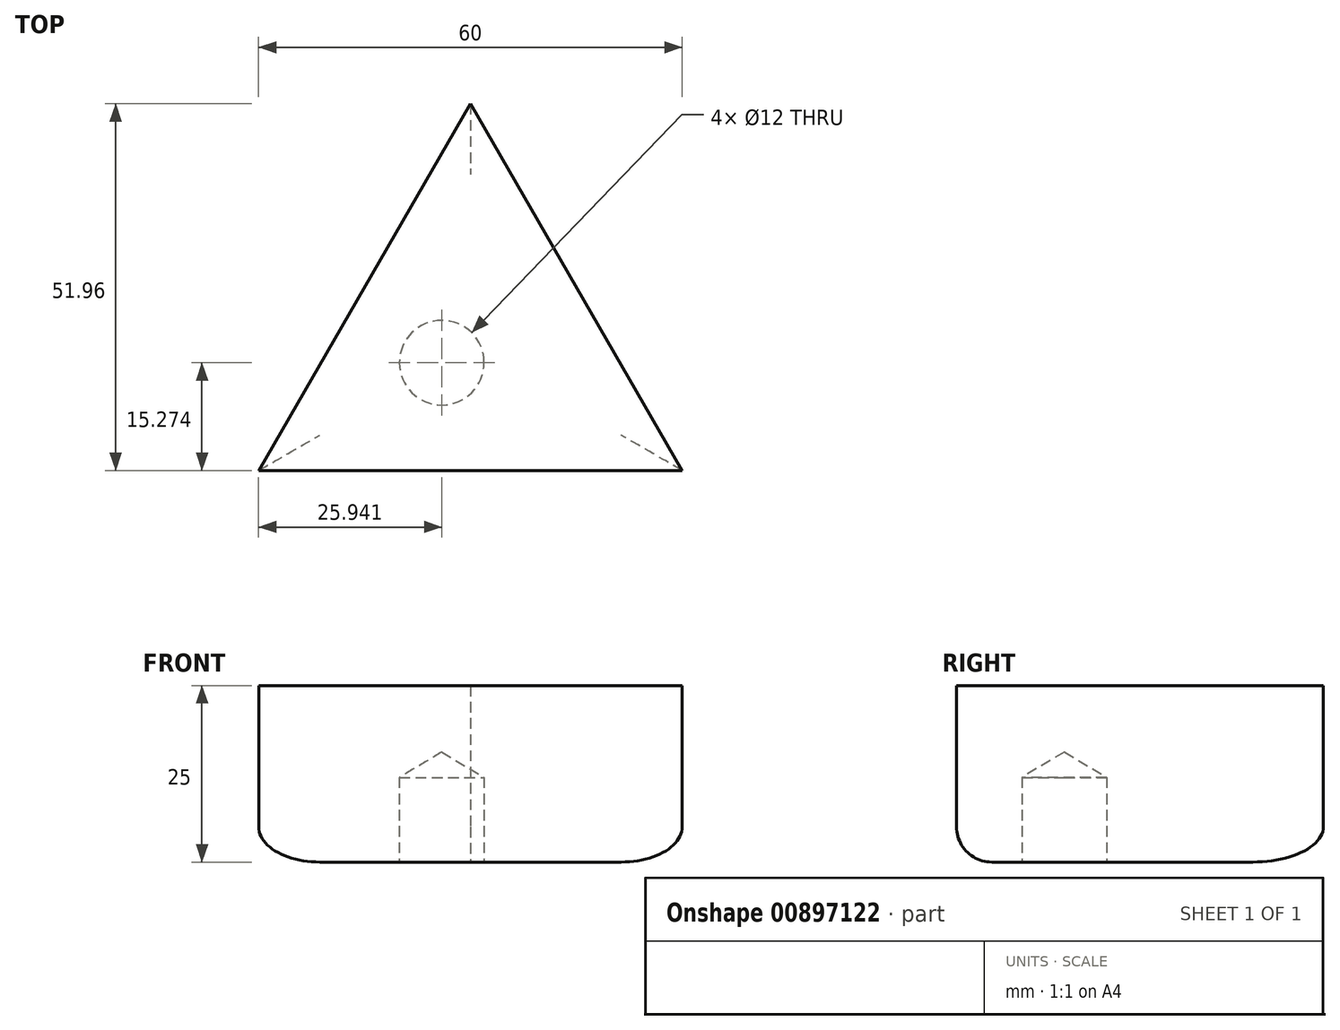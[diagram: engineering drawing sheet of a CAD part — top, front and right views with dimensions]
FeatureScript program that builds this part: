
annotation { "Feature Type Name" : "Feature", "Feature Type Description" : "" }
export const myFeature = defineFeature(function(context is Context, id is Id, definition is map)
    precondition{}
    {
        {
            var Q0;
            Q0=qCreatedBy(makeId("Top.planeOp"),FACE);
            var sketch = newSketch(context, id + "F0", { "sketchPlane" : qUnion([Q0])});
            skLineSegment(sketch, "E0", {"start": v(-14.06, 34.52) * mm, "end": v(-44.06, -17.44) * mm});
            skLineSegment(sketch, "E1", {"start": v(-44.06, -17.44) * mm, "end": v(15.94, -17.44) * mm});
            skLineSegment(sketch, "E2", {"start": v(15.94, -17.44) * mm, "end": v(-14.06, 34.52) * mm});
            skLineSegment(sketch, "E3", {"start": v(0.94, 8.54) * mm, "end": v(-44.06, -17.44) * mm, "construction": true});
            skLineSegment(sketch, "E4", {"start": v(-14.06, 34.52) * mm, "end": v(-21.56, -4.45) * mm, "construction": true});
            skLineSegment(sketch, "E5", {"start": v(-21.56, -4.45) * mm, "end": v(15.94, -17.44) * mm, "construction": true});
            skCircle(sketch, "E6", {"center": v(-21.56, -4.45) * mm, "radius": 7.39 * mm});
            skSolve(sketch);
        }
        {
            var Q0;
            Q0 = qSketchRegion(id + "F0", true);
            var Q1;
            Q1=makeQuery(id+"F0.imprint","IMPRINT",FACE,{"disambiguationData":[TD([[makeQuery(id+"F0.imprint","IMPRINT",EDGE,{"derivedFrom":sQuery(id+"F0.wireOp",EDGE,"E6")}),1.0]])]});
            extrude(context, id + "F1", {"entities" : qUnion([Q0, Q1]), "depth" : 25 * mm, "offsetDistance" : 25 * mm});
        }
        {
            var Q0;
            Q0=qCreatedBy(makeId("Top.planeOp"),FACE);
            var sketch = newSketch(context, id + "F2", { "sketchPlane" : qUnion([Q0])});
            skCircle(sketch, "E7", {"center": v(-18.12, -2.17) * mm, "radius": 6.2 * mm});
            skSolve(sketch);
        }
        {
            var Q0;
            Q0=sQuery(id+"F2.wireOp",VERTEX,"E7.center");
            var Q1;
            Q1=makeQuery(id+"F1.opExtrude","SWEPT_BODY",BODY,{"disambiguationData":[OSD([sQuery(id+"F0.wireOp",EDGE,"E0"),sQuery(id+"F0.wireOp",EDGE,"E1"),sQuery(id+"F0.wireOp",EDGE,"E2")])]});
            hole(context, id + "F3", {"style" : HoleStyle.SIMPLE, "endStyle" : HoleEndStyle.BLIND, "oppositeDirection" : true, "holeDiameter" : 12 * mm, "majorDiameter" : 5 * mm, "holeDepth" : 12 * mm, "isTappedThrough" : true, "tappedDepth" : 12 * mm, "tapClearance" : 3, "locations" : qUnion([Q0]), "scope" : qUnion([Q1])});
        }
        {
            var Q0;
            Q0=makeQuery(id+"F1.opExtrude","CAP_EDGE",EDGE,{"disambiguationData":[OSD([sQuery(id+"F0.wireOp",EDGE,"E2")])],"isStart":true});
            var Q1;
            Q1=makeQuery(id+"F1.opExtrude","CAP_EDGE",EDGE,{"disambiguationData":[OSD([sQuery(id+"F0.wireOp",EDGE,"E1")])],"isStart":true});
            var Q2;
            Q2=makeQuery(id+"F1.opExtrude","CAP_EDGE",EDGE,{"disambiguationData":[OSD([sQuery(id+"F0.wireOp",EDGE,"E0")])],"isStart":true});
            fillet(context, id + "F4", {"entities" : qUnion([Q0, Q1, Q2]), "radius" : 5 * mm, "tangentPropagation" : true, "allowEdgeOverflow" : false});
        }
    });
